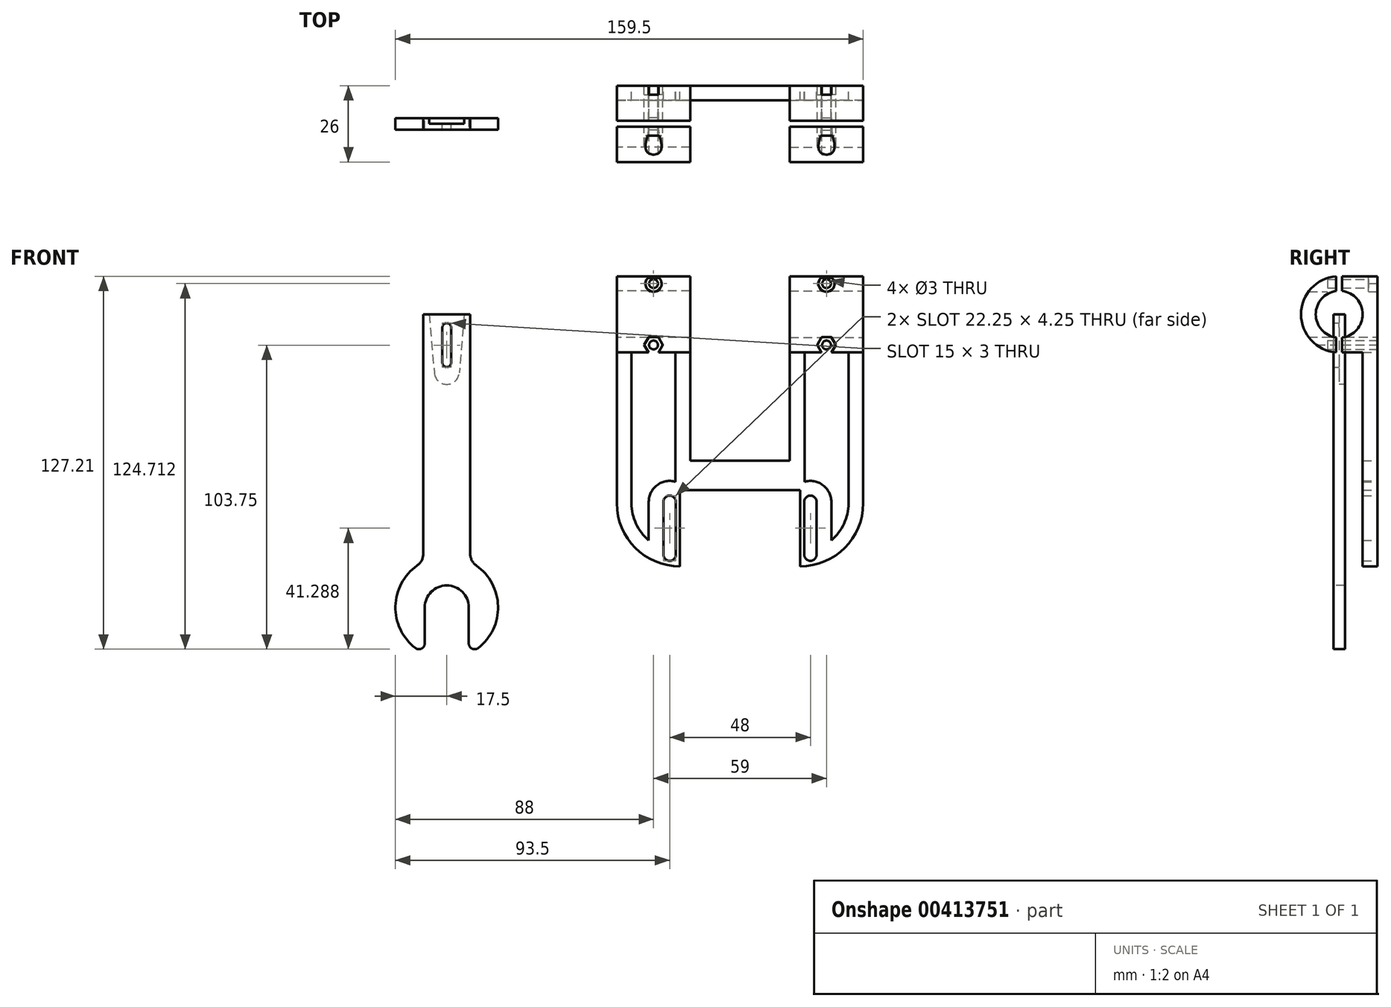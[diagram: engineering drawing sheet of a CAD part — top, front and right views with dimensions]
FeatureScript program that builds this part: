
annotation { "Feature Type Name" : "Feature", "Feature Type Description" : "" }
export const myFeature = defineFeature(function(context is Context, id is Id, definition is map)
    precondition{}
    {
        {
            var Q0;
            Q0=qCreatedBy(makeId("Right.planeOp"),FACE);
            var sketch = newSketch(context, id + "F0", { "sketchPlane" : qUnion([Q0])});
            skArc(sketch, "E0", {"start": v(1, -7.94) * mm, "mid": v(8, 0) * mm, "end": v(1, 7.94) * mm});
            skArc(sketch, "E1.0", {"start": v(1, -12.96) * mm, "mid": v(13, 0) * mm, "end": v(1, 12.96) * mm, "construction": true});
            skLineSegment(sketch, "E2", {"start": v(0, 16.35) * mm, "end": v(0, -17.05) * mm, "construction": true});
            skLineSegment(sketch, "E3.0", {"start": v(-1, 12.96) * mm, "end": v(-1, 7.94) * mm});
            skLineSegment(sketch, "E4.0", {"start": v(1, 12.96) * mm, "end": v(1, 7.94) * mm});
            skArc(sketch, "E5.trimOffspring", {"start": v(-1, 7.94) * mm, "mid": v(-8, 0) * mm, "end": v(-1, -7.94) * mm});
            skArc(sketch, "E6.trimOffspring", {"start": v(-1, 12.96) * mm, "mid": v(-13, 0) * mm, "end": v(-1, -12.96) * mm});
            skLineSegment(sketch, "E7.trimOffspring", {"start": v(-1, -7.94) * mm, "end": v(-1, -12.96) * mm});
            skLineSegment(sketch, "E8.trimOffspring", {"start": v(1, -7.94) * mm, "end": v(1, -12.96) * mm});
            skLineSegment(sketch, "E9", {"start": v(1, 12.96) * mm, "end": v(13, 12.96) * mm});
            skPoint(sketch, "E9.endSnap0", {"position": v(13, 0) * mm});
            skLineSegment(sketch, "E10", {"start": v(13, 12.96) * mm, "end": v(13, -12.96) * mm});
            skLineSegment(sketch, "E11", {"start": v(13, -12.96) * mm, "end": v(1, -12.96) * mm});
            skSolve(sketch);
        }
        {
            var Q0;
            Q0=makeQuery(id+"F0.imprint","IMPRINT",FACE,{"disambiguationData":[TD([[makeQuery(id+"F0.imprint","IMPRINT",EDGE,{"derivedFrom":sQuery(id+"F0.wireOp",EDGE,"E3.0")}),-1.0]])]});
            var Q1;
            Q1=makeQuery(id+"F0.imprint","IMPRINT",FACE,{"disambiguationData":[TD([[makeQuery(id+"F0.imprint","IMPRINT",EDGE,{"derivedFrom":sQuery(id+"F0.wireOp",EDGE,"E0")}),-1.0]])]});
            extrude(context, id + "F1", {"entities" : qUnion([Q0, Q1]), "depth" : 25 * mm});
        }
        {
            var Q0;
            {var subQ0=sQuery(id+"F0.wireOp",EDGE,"E10");Q0=makeQuery(id+"FDwyYTMkyQEUwtv_2.boolean.opBoolean","MERGE",FACE,{"derivedFrom":[makeQuery(id+"F1.opExtrude","SWEPT_FACE",FACE,{"disambiguationData":[OSD([subQ0])]}),makeQuery(id+"FDwyYTMkyQEUwtv_2.opExtrude","CAP_FACE",FACE,{"disambiguationData":[OSD([subQ0,sQuery(id+"FfCzFZaleCxli49_2.wireOp",EDGE,"xbniV7xK-1MVI-rtrQ-LqnJ-8gcfz6MUxPXB"),sQuery(id+"FfCzFZaleCxli49_2.wireOp",EDGE,"VkD3Inu4-AVyj-rKwd-6Fpr-5A2urvKLaV5Z"),sQuery(id+"FfCzFZaleCxli49_2.wireOp",EDGE,"fe516dc2-f1ae-47a2-9d52-99eedcf993a5"),sQuery(id+"FfCzFZaleCxli49_2.wireOp",EDGE,"337c6c97-f909-42ce-a29d-4f2d60a9197b")])],"isStart":true})]});}
            var sketch = newSketch(context, id + "F2", { "sketchPlane" : qUnion([Q0])});
            skLineSegment(sketch, "E12", {"start": v(0, 10.46) * mm, "end": v(-25, 10.46) * mm, "construction": true});
            skCircle(sketch, "E13.cCircle", {"center": v(-12.5, 10.46) * mm, "radius": 2.75 * mm, "construction": true});
            skLineSegment(sketch, "E13.0", {"start": v(-10.91, 7.71) * mm, "end": v(-14.09, 7.71) * mm});
            skLineSegment(sketch, "E13.1", {"start": v(-14.09, 7.71) * mm, "end": v(-15.68, 10.46) * mm});
            skLineSegment(sketch, "E13.2", {"start": v(-15.68, 10.46) * mm, "end": v(-14.09, 13.21) * mm});
            skLineSegment(sketch, "E13.3", {"start": v(-14.09, 13.21) * mm, "end": v(-10.91, 13.21) * mm});
            skLineSegment(sketch, "E13.4", {"start": v(-10.91, 13.21) * mm, "end": v(-9.32, 10.46) * mm});
            skLineSegment(sketch, "E13.5", {"start": v(-9.32, 10.46) * mm, "end": v(-10.91, 7.71) * mm});
            skPoint(sketch, "E13.0.midPoint", {"position": v(-12.5, 7.71) * mm});
            skCircle(sketch, "E14", {"center": v(-12.5, 10.46) * mm, "radius": 1.5 * mm});
            skLineSegment(sketch, "E15.MirrorCS", {"start": v(-10.91, -7.71) * mm, "end": v(-14.09, -7.71) * mm});
            skLineSegment(sketch, "E16.MirrorCS", {"start": v(-14.09, -7.71) * mm, "end": v(-15.68, -10.46) * mm});
            skLineSegment(sketch, "E17.MirrorCS", {"start": v(-15.68, -10.46) * mm, "end": v(-14.09, -13.21) * mm});
            skLineSegment(sketch, "E18.MirrorCS", {"start": v(-14.09, -13.21) * mm, "end": v(-10.91, -13.21) * mm});
            skLineSegment(sketch, "E19.MirrorCS", {"start": v(-10.91, -13.21) * mm, "end": v(-9.32, -10.46) * mm});
            skLineSegment(sketch, "E20.MirrorCS", {"start": v(-9.32, -10.46) * mm, "end": v(-10.91, -7.71) * mm});
            skCircle(sketch, "E21.MirrorC", {"center": v(-12.5, -10.46) * mm, "radius": 1.5 * mm});
            skSolve(sketch);
        }
        {
            var Q0;
            Q0=makeQuery(id+"F2.imprint","IMPRINT",FACE,{"disambiguationData":[TD([[makeQuery(id+"F2.imprint","IMPRINT",EDGE,{"derivedFrom":sQuery(id+"F2.wireOp",EDGE,"E14")}),1.0]])]});
            var Q1;
            Q1=makeQuery(id+"F2.imprint","IMPRINT",FACE,{"disambiguationData":[TD([[makeQuery(id+"F2.imprint","IMPRINT",EDGE,{"derivedFrom":sQuery(id+"F2.wireOp",EDGE,"E21.MirrorC")}),-1.0]])]});
            extrude(context, id + "F3", {"entities" : qUnion([Q0, Q1]), "operationType" : NewBodyOperationType.REMOVE, "endBound" : BoundingType.THROUGH_ALL, "oppositeDirection" : true, "depth" : 25 * mm});
        }
        {
            var Q0;
            Q0=makeQuery(id+"F2.imprint","IMPRINT",FACE,{"disambiguationData":[TD([[makeQuery(id+"F2.imprint","IMPRINT",EDGE,{"derivedFrom":sQuery(id+"F2.wireOp",EDGE,"E13.0")}),-1.0]])]});
            var Q1;
            Q1=makeQuery(id+"F2.imprint","IMPRINT",FACE,{"disambiguationData":[TD([[makeQuery(id+"F2.imprint","IMPRINT",EDGE,{"derivedFrom":sQuery(id+"F2.wireOp",EDGE,"E15.MirrorCS")}),1.0]])]});
            extrude(context, id + "F4", {"entities" : qUnion([Q0, Q1]), "operationType" : NewBodyOperationType.REMOVE, "oppositeDirection" : true, "depth" : 3 * mm});
        }
        {
            var Q0;
            Q0=makeQuery(id+"F1.opExtrude","SWEPT_FACE",FACE,{"disambiguationData":[OSD([sQuery(id+"F0.wireOp",EDGE,"E3.0")])]});
            var sketch = newSketch(context, id + "F5", { "sketchPlane" : qUnion([Q0])});
            skCircle(sketch, "E22", {"center": v(-12.5, 10.46) * mm, "radius": 2.75 * mm});
            skCircle(sketch, "E23.0", {"center": v(-12.5, -10.46) * mm, "radius": 1.5 * mm, "construction": true});
            skCircle(sketch, "E24", {"center": v(-12.5, -10.46) * mm, "radius": 2.75 * mm});
            skSolve(sketch);
        }
        {
            var Q0;
            {var subQ1=sQuery(id+"F0.wireOp",EDGE,"E3.0");Q0=makeQuery(id+"F5.imprint","IMPRINT",FACE,{"disambiguationData":[TD([[makeQuery(id+"F5.imprint","IMPRINT",EDGE,{"derivedFrom":makeQuery(id+"F3.boolean.opBoolean","INTERSECT",EDGE,{"derivedFrom":[makeQuery(id+"F1.opExtrude","SWEPT_FACE",FACE,{"disambiguationData":[OSD([subQ1])]}),makeQuery(id+"F3.opExtrude","SWEPT_FACE",FACE,{"disambiguationData":[OSD([sQuery(id+"F2.wireOp",EDGE,"E14")])]})]})}),-1.0]])]});}
            var Q1;
            Q1=makeQuery(id+"F5.imprint","IMPRINT",FACE,{"disambiguationData":[TD([[makeQuery(id+"F5.imprint","IMPRINT",EDGE,{"derivedFrom":sQuery(id+"F5.wireOp",EDGE,"E24")}),1.0]])]});
            var Q2;
            {var subQ0=sQuery(id+"F5.wireOp",EDGE,"E22");var subQ1=makeQuery(id+"F1.opExtrude","SWEPT_EDGE",EDGE,{"disambiguationData":[OSD([sQuery(id+"F0.wireOp",EDGE,"E3.0"),sQuery(id+"F0.wireOp",EDGE,"E5.trimOffspring")])]});var subQ2=makeQuery(id+"F5.imprint","INTERSECT",VERTEX,{"disambiguationData":[OD(0.0)],"derivedFrom":[subQ1,subQ0]});Q2=makeQuery(id+"F5.imprint","IMPRINT",FACE,{"disambiguationData":[TD([[makeQuery(id+"F5.imprint","IMPRINT",EDGE,{"disambiguationData":[TD([[subQ2,-1.0]])],"derivedFrom":subQ0}),1.0]])]});}
            extrude(context, id + "F6", {"entities" : qUnion([Q0, Q1, Q2]), "operationType" : NewBodyOperationType.REMOVE, "endBound" : BoundingType.THROUGH_ALL, "oppositeDirection" : true, "depth" : 10.56 * mm, "hasSecondDirection" : true, "secondDirectionOppositeDirection" : true, "secondDirectionDepth" : 3 * mm});
        }
        {
            var Q0;
            Q0=makeQuery(id+"F1.opExtrude","SWEPT_FACE",FACE,{"disambiguationData":[OSD([sQuery(id+"F0.wireOp",EDGE,"E10")])]});
            var sketch = newSketch(context, id + "F7", { "sketchPlane" : qUnion([Q0])});
            skLineSegment(sketch, "E25", {"start": v(-25, 12.96) * mm, "end": v(-42, 12.96) * mm});
            skLineSegment(sketch, "E26", {"start": v(-42, 12.96) * mm, "end": v(-42, -12.96) * mm});
            skLineSegment(sketch, "E27", {"start": v(-42, -12.96) * mm, "end": v(-25, -12.96) * mm});
            skSolve(sketch);
        }
        {
            var Q0;
            Q0=qCreatedBy(makeId("Right.planeOp"),FACE);
            var Q1;
            Q1=sQuery(id+"F7.wireOp",VERTEX,"E26.start");
            cPlane(context, id + "F8", {"entities" : qUnion([Q0, Q1]), "cplaneType" : CPlaneType.PLANE_POINT, "offset" : 46.68 * mm, "width" : 150 * mm, "height" : 150 * mm});
        }
        {
            var Q0;
            Q0=makeQuery(id+"F1.opExtrude","SWEPT_BODY",BODY,{"disambiguationData":[OSD([sQuery(id+"F0.wireOp",EDGE,"E3.0"),sQuery(id+"F0.wireOp",EDGE,"E5.trimOffspring"),sQuery(id+"F0.wireOp",EDGE,"E6.trimOffspring"),sQuery(id+"F0.wireOp",EDGE,"E7.trimOffspring")])]});
            var Q1;
            Q1=makeQuery(id+"F1.opExtrude","SWEPT_BODY",BODY,{"disambiguationData":[OSD([sQuery(id+"F0.wireOp",EDGE,"E0"),sQuery(id+"F0.wireOp",EDGE,"E4.0"),sQuery(id+"F0.wireOp",EDGE,"E8.trimOffspring"),sQuery(id+"F0.wireOp",EDGE,"E9"),sQuery(id+"F0.wireOp",EDGE,"E10"),sQuery(id+"F0.wireOp",EDGE,"E11")])]});
            var Q2;
            Q2=qCreatedBy(id+"F8.planeOp",FACE);
            mirror(context, id + "F9", {"entities" : qUnion([Q0, Q1]), "mirrorPlane" : qUnion([Q2])});
        }
        {
            var Q0;
            Q0=makeQuery(id+"F1.opExtrude","SWEPT_FACE",FACE,{"disambiguationData":[OSD([sQuery(id+"F0.wireOp",EDGE,"E10")])]});
            var sketch = newSketch(context, id + "F10", { "sketchPlane" : qUnion([Q0])});
            skPoint(sketch, "E28.0", {"position": v(-59, 12.96) * mm});
            skLineSegment(sketch, "E29.bottom", {"start": v(-25, -12.96) * mm, "end": v(-59, -12.96) * mm});
            skLineSegment(sketch, "E29.top", {"start": v(-25, 12.96) * mm, "end": v(-59, 12.96) * mm});
            skLineSegment(sketch, "E29.left", {"start": v(-25, -12.96) * mm, "end": v(-25, 12.96) * mm});
            skLineSegment(sketch, "E29.right", {"start": v(-59, -12.96) * mm, "end": v(-59, 12.96) * mm});
            skLineSegment(sketch, "E30", {"start": v(-59, -7.96) * mm, "end": v(-25, -7.96) * mm, "construction": true});
            skLineSegment(sketch, "E31", {"start": v(-42, -12.96) * mm, "end": v(-42, -72.96) * mm, "construction": true});
            skLineSegment(sketch, "E32.bottom", {"start": v(-21.5, -85.96) * mm, "end": v(-62.5, -85.96) * mm});
            skLineSegment(sketch, "E32.top", {"start": v(-21.5, -59.96) * mm, "end": v(-62.5, -59.96) * mm});
            skLineSegment(sketch, "E32.left", {"start": v(-21.5, -85.96) * mm, "end": v(-21.5, -59.96) * mm});
            skLineSegment(sketch, "E32.right", {"start": v(-62.5, -85.96) * mm, "end": v(-62.5, -59.96) * mm});
            skPoint(sketch, "E32.middle", {"position": v(-42, -72.96) * mm});
            skPoint(sketch, "E33.0", {"position": v(-84, -12.96) * mm});
            skPoint(sketch, "E34.0", {"position": v(0, -12.96) * mm});
            skArc(sketch, "E35", {"start": v(-62.5, -85.96) * mm, "mid": v(-77.7, -79.66) * mm, "end": v(-84, -64.46) * mm});
            skLineSegment(sketch, "E36", {"start": v(-84, -12.96) * mm, "end": v(-84, -64.46) * mm});
            skArc(sketch, "E37", {"start": v(-21.5, -85.96) * mm, "mid": v(-6.3, -79.66) * mm, "end": v(0, -64.46) * mm});
            skLineSegment(sketch, "E38", {"start": v(0, -12.96) * mm, "end": v(0, -64.46) * mm});
            skLineSegment(sketch, "E39", {"start": v(-84, -12.96) * mm, "end": v(-59, -12.96) * mm});
            skLineSegment(sketch, "E40", {"start": v(0, -12.96) * mm, "end": v(-25, -12.96) * mm});
            skLineSegment(sketch, "E41", {"start": v(-25, -12.96) * mm, "end": v(-25, -49.96) * mm});
            skLineSegment(sketch, "E42", {"start": v(-25, -49.96) * mm, "end": v(-59, -49.96) * mm});
            skLineSegment(sketch, "E43", {"start": v(-59, -49.96) * mm, "end": v(-59, -12.96) * mm});
            skLineSegment(sketch, "E44", {"start": v(-18, -72.96) * mm, "end": v(-66, -72.96) * mm, "construction": true});
            skLineSegment(sketch, "E45", {"start": v(-18, -63.96) * mm, "end": v(-18, -81.96) * mm, "construction": true});
            skArc(sketch, "E46.0.startCap", {"start": v(-20.13, -63.96) * mm, "mid": v(-18, -61.84) * mm, "end": v(-15.88, -63.96) * mm});
            skArc(sketch, "E46.0.endCap", {"start": v(-15.87, -81.96) * mm, "mid": v(-18, -84.09) * mm, "end": v(-20.12, -81.96) * mm});
            skLineSegment(sketch, "E46.0.left", {"start": v(-15.88, -63.96) * mm, "end": v(-15.88, -81.96) * mm});
            skLineSegment(sketch, "E46.0.right", {"start": v(-20.13, -63.96) * mm, "end": v(-20.13, -81.96) * mm});
            skLineSegment(sketch, "E47.MirrorCS", {"start": v(-63.88, -63.96) * mm, "end": v(-63.88, -81.96) * mm});
            skLineSegment(sketch, "E48.MirrorCS", {"start": v(-68.12, -63.96) * mm, "end": v(-68.12, -81.96) * mm});
            skArc(sketch, "E49.MirrorCS", {"start": v(-68.12, -81.96) * mm, "mid": v(-66, -84.09) * mm, "end": v(-63.88, -81.96) * mm});
            skArc(sketch, "E50.MirrorCS", {"start": v(-63.88, -63.96) * mm, "mid": v(-66, -61.84) * mm, "end": v(-68.12, -63.96) * mm});
            skArc(sketch, "E51.0", {"start": v(-21.5, -80.96) * mm, "mid": v(-18.64, -80.71) * mm, "end": v(-15.88, -79.97) * mm, "construction": true});
            skLineSegment(sketch, "E51.1", {"start": v(-5, -17.96) * mm, "end": v(-5, -64.46) * mm});
            skLineSegment(sketch, "E51.3", {"start": v(-20, -17.96) * mm, "end": v(-20, -49.96) * mm});
            skLineSegment(sketch, "E52.0", {"start": v(-10.88, -63.96) * mm, "end": v(-10.88, -77.09) * mm});
            skArc(sketch, "E52.1", {"start": v(-25.12, -63.96) * mm, "mid": v(-24.81, -61.87) * mm, "end": v(-23.9, -59.96) * mm, "construction": true});
            skArc(sketch, "E53.trimOffspring", {"start": v(-10.88, -77.09) * mm, "mid": v(-6.54, -71.42) * mm, "end": v(-5, -64.46) * mm});
            skLineSegment(sketch, "E54", {"start": v(-20, -49.96) * mm, "end": v(-20, -57.12) * mm});
            skArc(sketch, "E55.trimOffspring", {"start": v(-20, -57.12) * mm, "mid": v(-13.73, -58.26) * mm, "end": v(-10.88, -63.96) * mm});
            skArc(sketch, "E56.MirrorCS", {"start": v(-73.12, -77.09) * mm, "mid": v(-77.46, -71.42) * mm, "end": v(-79, -64.46) * mm});
            skLineSegment(sketch, "E57.MirrorCS", {"start": v(-73.12, -63.96) * mm, "end": v(-73.12, -77.09) * mm});
            skArc(sketch, "E58.MirrorCS", {"start": v(-64, -57.12) * mm, "mid": v(-70.27, -58.26) * mm, "end": v(-73.12, -63.96) * mm});
            skLineSegment(sketch, "E59.MirrorCS", {"start": v(-64, -49.96) * mm, "end": v(-64, -57.12) * mm});
            skLineSegment(sketch, "E60.MirrorCS", {"start": v(-64, -17.96) * mm, "end": v(-64, -49.96) * mm});
            skLineSegment(sketch, "E61.MirrorCS", {"start": v(-79, -17.96) * mm, "end": v(-79, -64.46) * mm});
            skLineSegment(sketch, "E62", {"start": v(-5, -17.96) * mm, "end": v(-5, -12.96) * mm});
            skLineSegment(sketch, "E63", {"start": v(-20, -17.96) * mm, "end": v(-20, -12.96) * mm});
            skLineSegment(sketch, "E64.MirrorCS", {"start": v(-64, -17.96) * mm, "end": v(-64, -12.96) * mm});
            skLineSegment(sketch, "E65.MirrorCS", {"start": v(-79, -17.96) * mm, "end": v(-79, -12.96) * mm});
            skSolve(sketch);
        }
        {
            var Q0;
            Q0=makeQuery(id+"F10.imprint","IMPRINT",FACE,{"disambiguationData":[TD([[makeQuery(id+"F10.imprint","IMPRINT",EDGE,{"derivedFrom":sQuery(id+"F10.wireOp",EDGE,"E32.top")}),-1.0]])]});
            extrude(context, id + "F11", {"entities" : qUnion([Q0]), "operationType" : NewBodyOperationType.ADD, "oppositeDirection" : true, "depth" : 5 * mm});
        }
        {
            var Q0;
            Q0=qCreatedBy(makeId("Front.planeOp"),FACE);
            var sketch = newSketch(context, id + "F12", { "sketchPlane" : qUnion([Q0])});
            skLineSegment(sketch, "E66.bottom", {"start": v(-66, 0) * mm, "end": v(-50, 0) * mm});
            skLineSegment(sketch, "E66.left", {"start": v(-66, 0) * mm, "end": v(-66, -81.64) * mm});
            skLineSegment(sketch, "E66.right", {"start": v(-50, 0) * mm, "end": v(-50, -81.64) * mm});
            skLineSegment(sketch, "E67", {"start": v(-64, 0) * mm, "end": v(-52, 0) * mm, "construction": true});
            skPoint(sketch, "E68", {"position": v(-58, 0) * mm});
            skLineSegment(sketch, "E69", {"start": v(-58, 0) * mm, "end": v(-58, -20) * mm, "construction": true});
            skLineSegment(sketch, "E70", {"start": v(-62.25, -20) * mm, "end": v(-53.75, -20) * mm, "construction": true});
            skLineSegment(sketch, "E71", {"start": v(-64, 0) * mm, "end": v(-62.25, -20) * mm});
            skLineSegment(sketch, "E72", {"start": v(-52, 0) * mm, "end": v(-53.75, -20) * mm});
            skArc(sketch, "E73", {"start": v(-62.25, -20) * mm, "mid": v(-58, -23.9) * mm, "end": v(-53.75, -20) * mm});
            skCircle(sketch, "E74", {"center": v(-58, -4.5) * mm, "radius": 1.5 * mm});
            skCircle(sketch, "E75.0.1.0", {"center": v(-58, -16.5) * mm, "radius": 1.5 * mm});
            skLineSegment(sketch, "E75.direction1", {"start": v(-58, -4.5) * mm, "end": v(-33, -4.5) * mm, "construction": true});
            skLineSegment(sketch, "E75.direction2", {"start": v(-58, -4.5) * mm, "end": v(-58, -16.5) * mm, "construction": true});
            skPoint(sketch, "E76.startSnap0", {"position": v(-58, -23.9) * mm});
            skLineSegment(sketch, "E77", {"start": v(-59.5, -4.5) * mm, "end": v(-59.5, -16.5) * mm});
            skLineSegment(sketch, "E78", {"start": v(-56.5, -16.5) * mm, "end": v(-56.5, -4.5) * mm});
            skArc(sketch, "E79", {"start": v(-50.5, -100) * mm, "mid": v(-58, -92.5) * mm, "end": v(-65.5, -100) * mm});
            skPoint(sketch, "E79.centerSnap0", {"position": v(-58, -120) * mm});
            skArc(sketch, "E80", {"start": v(-50.5, -115.81) * mm, "mid": v(-40.57, -101.51) * mm, "end": v(-47.89, -85.72) * mm});
            skPoint(sketch, "E81.orphan", {"position": v(-50, -120) * mm});
            skPoint(sketch, "E82.trimOffspring.end.orphan", {"position": v(-66, -120) * mm});
            skLineSegment(sketch, "E83", {"start": v(-65.5, -100) * mm, "end": v(-65.5, -115.81) * mm});
            skLineSegment(sketch, "E84", {"start": v(-50.5, -100) * mm, "end": v(-50.5, -115.81) * mm});
            skArc(sketch, "E85.trimOffspring", {"start": v(-68.11, -85.72) * mm, "mid": v(-75.43, -101.51) * mm, "end": v(-65.5, -115.81) * mm});
            skPoint(sketch, "E86.visualSharp", {"position": v(-50, -84.44) * mm});
            skArc(sketch, "E86.filletArc", {"start": v(-50, -81.64) * mm, "mid": v(-49.44, -83.93) * mm, "end": v(-47.89, -85.72) * mm});
            skPoint(sketch, "E87.visualSharp", {"position": v(-66, -84.44) * mm});
            skArc(sketch, "E87.filletArc", {"start": v(-68.11, -85.72) * mm, "mid": v(-66.56, -83.93) * mm, "end": v(-66, -81.64) * mm});
            skSolve(sketch);
        }
        {
            var Q0;
            {var subQ3=sQuery(id+"F12.wireOp",EDGE,"E66.left");Q0=makeQuery(id+"F12.imprint","IMPRINT",FACE,{"disambiguationData":[TD([[makeQuery(id+"F12.imprint","IMPRINT",EDGE,{"derivedFrom":subQ3}),1.0]])]});}
            extrude(context, id + "F13", {"entities" : qUnion([Q0]), "oppositeDirection" : true, "depth" : 2 * mm});
        }
        {
            var Q0;
            {var subQ3=sQuery(id+"F12.wireOp",EDGE,"E66.left");Q0=makeQuery(id+"F12.imprint","IMPRINT",FACE,{"disambiguationData":[TD([[makeQuery(id+"F12.imprint","IMPRINT",EDGE,{"derivedFrom":subQ3}),1.0]])]});}
            var Q1;
            {var subQ1=sQuery(id+"F12.wireOp",EDGE,"E71");Q1=makeQuery(id+"F12.imprint","IMPRINT",FACE,{"disambiguationData":[TD([[makeQuery(id+"F12.imprint","IMPRINT",EDGE,{"derivedFrom":subQ1}),1.0]])]});}
            extrude(context, id + "F14", {"entities" : qUnion([Q0, Q1]), "operationType" : NewBodyOperationType.ADD, "depth" : 2 * mm});
        }
        {
            var Q0;
            {var subQ0=sQuery(id+"F12.wireOp",EDGE,"E85.trimOffspring");var subQ1=sQuery(id+"F12.wireOp",EDGE,"E83");Q0=makeQuery(id+"F14.boolean.opBoolean","MERGE",EDGE,{"derivedFrom":[makeQuery(id+"F13.opExtrude","SWEPT_EDGE",EDGE,{"disambiguationData":[OSD([subQ1,subQ0])]}),makeQuery(id+"F14.opExtrude","SWEPT_EDGE",EDGE,{"disambiguationData":[OSD([subQ1,subQ0])]})]});}
            var Q1;
            {var subQ0=sQuery(id+"F12.wireOp",EDGE,"E84");var subQ1=sQuery(id+"F12.wireOp",EDGE,"E80");Q1=makeQuery(id+"F14.boolean.opBoolean","MERGE",EDGE,{"derivedFrom":[makeQuery(id+"F13.opExtrude","SWEPT_EDGE",EDGE,{"disambiguationData":[OSD([subQ1,subQ0])]}),makeQuery(id+"F14.opExtrude","SWEPT_EDGE",EDGE,{"disambiguationData":[OSD([subQ1,subQ0])]})]});}
            fillet(context, id + "F15", {"entities" : qUnion([Q0, Q1]), "radius" : 2 * mm, "tangentPropagation" : true, "allowEdgeOverflow" : false});
        }
    });
